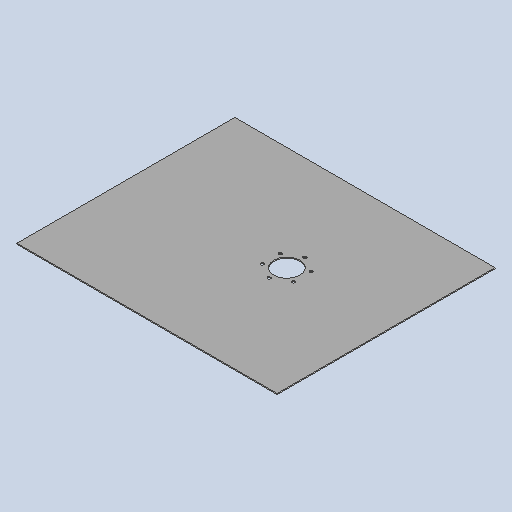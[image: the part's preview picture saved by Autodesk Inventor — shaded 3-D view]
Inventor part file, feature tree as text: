
AUTODESK INVENTOR PART (.ipt)
format: ipt  version: 2025 (Build 290162010, 162A)  size: 289,280 bytes
history: native  units: mm
features: other x5, sketch x3, sheet_metal_op x1, pattern_circular x1
ambient origin geometry x8: Origin, YZ Plane, XZ Plane, XY Plane, X Axis, Y Axis, Z Axis, Center Point
bodies: Solid1 (feature_tree)
feature tree (10):
  sheet_metal_op  "Face1"
  other  "Mark1"
  other  "A-Side Definition"
  pattern_circular  "Circular Pattern1"  Count=20  [1 undecoded]
  sketch  "Sketch1"  dims[d2=3.0mm d6=200.0mm]
  other  "Plate1"
  sketch  "Sketch2"  dims[d9=20.0mm]
  sketch  "Sketch3"  dims[d10=20.0mm d11=20.0mm d14=80.0mm d15=320.0mm d17=320.0mm d19=10.0mm d20=55.0mm d21=3.0mm d22=0.0mm d23=60.0mm d24=360.0deg d26=800.0mm d27=670.0mm]
  other  "Cut1"
  other  "Definition1"
note: 1 required parameter value undecoded (feature->parameter linkage not recoverable at this tier; creation-order binding heuristic only, values carry confidence <= 0.55)
